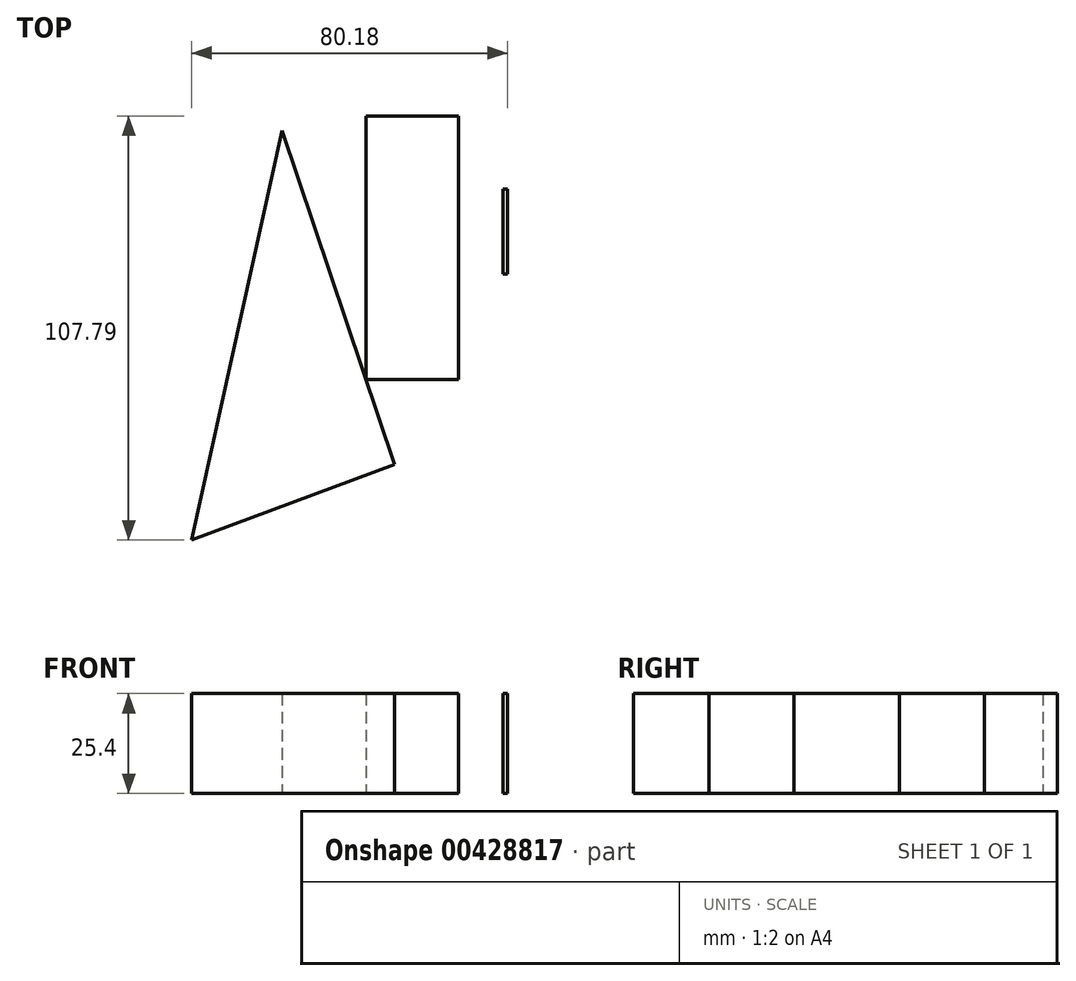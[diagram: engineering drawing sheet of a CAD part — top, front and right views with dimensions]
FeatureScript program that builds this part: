
annotation { "Feature Type Name" : "Feature", "Feature Type Description" : "" }
export const myFeature = defineFeature(function(context is Context, id is Id, definition is map)
    precondition{}
    {
        {
            var Q0;
            Q0=qCreatedBy(makeId("Top.planeOp"),FACE);
            var sketch = newSketch(context, id + "F0", { "sketchPlane" : qUnion([Q0])});
            skLineSegment(sketch, "E0", {"start": v(52.18, 0) * mm, "end": v(89.04, -109) * mm});
            skLineSegment(sketch, "E1", {"start": v(89.04, -109) * mm, "end": v(60.35, -24.14) * mm});
            skLineSegment(sketch, "E2", {"start": v(60.35, -24.14) * mm, "end": v(37.48, -128.23) * mm});
            skLineSegment(sketch, "E3", {"start": v(37.48, -128.23) * mm, "end": v(89.04, -109) * mm});
            skLineSegment(sketch, "E4.bottom", {"start": v(117.66, -60.63) * mm, "end": v(116.5, -60.63) * mm});
            skLineSegment(sketch, "E4.top", {"start": v(117.66, -39.05) * mm, "end": v(116.5, -39.05) * mm});
            skLineSegment(sketch, "E4.left", {"start": v(117.66, -60.63) * mm, "end": v(117.66, -39.05) * mm});
            skLineSegment(sketch, "E4.right", {"start": v(116.5, -60.63) * mm, "end": v(116.5, -39.05) * mm});
            skLineSegment(sketch, "E5.bottom", {"start": v(105.27, -20.44) * mm, "end": v(81.75, -20.44) * mm});
            skLineSegment(sketch, "E5.top", {"start": v(105.27, -87.44) * mm, "end": v(81.75, -87.44) * mm});
            skLineSegment(sketch, "E5.left", {"start": v(105.27, -20.44) * mm, "end": v(105.27, -87.44) * mm});
            skLineSegment(sketch, "E5.right", {"start": v(81.75, -20.44) * mm, "end": v(81.75, -87.44) * mm});
            skSolve(sketch);
        }
        {
            var Q0;
            Q0 = qSketchRegion(id + "F0", true);
            extrude(context, id + "F1", {"entities" : qUnion([Q0]), "depth" : 25.4 * mm});
        }
    });
